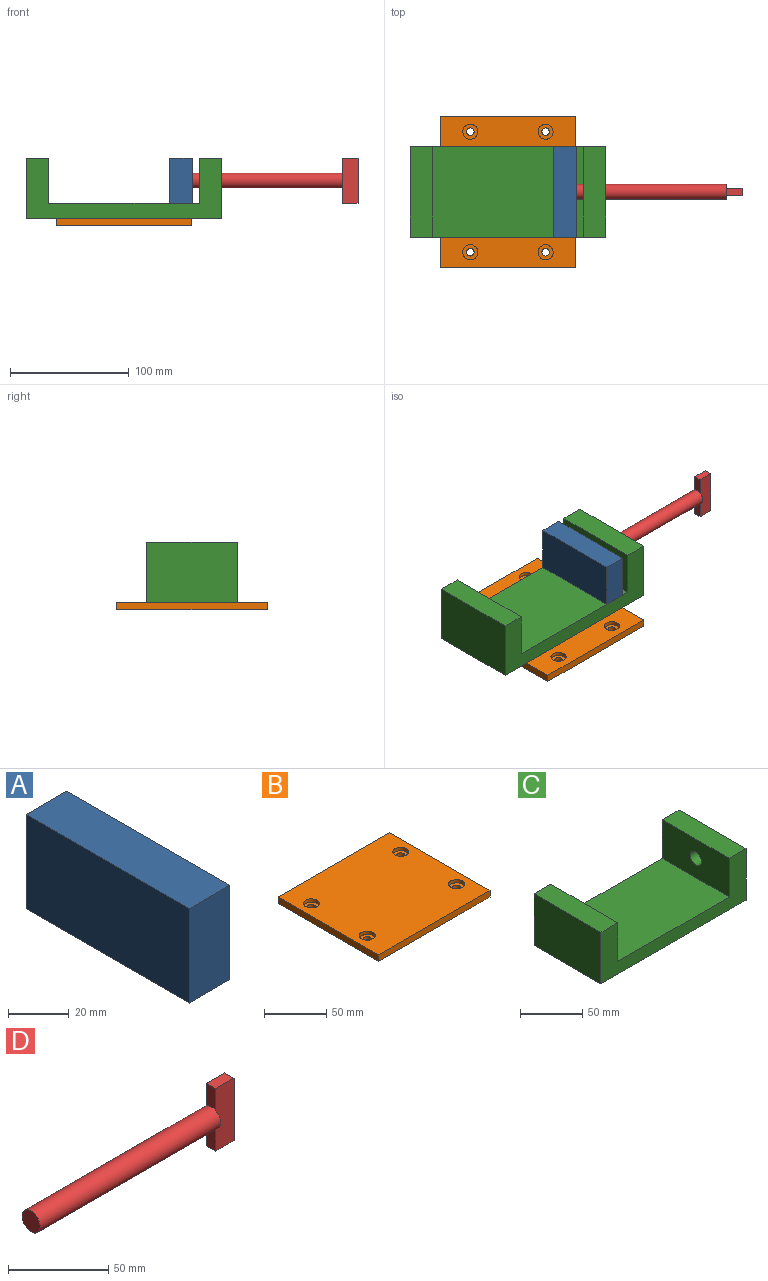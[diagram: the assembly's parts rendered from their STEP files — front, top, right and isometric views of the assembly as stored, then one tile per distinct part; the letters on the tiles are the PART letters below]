
ASSEMBLY  parts=4 mates=4
PART A: 6 faces, bbox 19.1x76.2x38.1 mm
  f0: plane 76.2x19.05mm, normal (0,0,1), area 1451.6mm2, adj f1,f3,f4,f5
  f1: plane 38.1x19.05mm, normal (0,-1,0), area 725.8mm2, adj f0,f2,f4,f5
  f2: plane 76.2x19.05mm, normal (0,0,-1), area 1451.6mm2, adj f1,f3,f4,f5
  f3: plane 38.1x19.05mm, normal (0,1,0), area 725.8mm2, adj f0,f2,f4,f5
  f4: plane 76.2x38.1mm, normal (1,0,0), area 2903.2mm2, adj f0,f1,f2,f3
  f5: plane 76.2x38.1mm, normal (-1,0,0), area 2903.2mm2, adj f0,f1,f2,f3
PART B: 18 faces, bbox 127x114.3x6.4 mm
  f0: plane 114.3x6.35mm, normal (-1,0,0), area 725.8mm2, adj f1,f3,f4,f5
  f1: plane 127x6.35mm, normal (0,-1,0), area 806.5mm2, adj f0,f2,f4,f5
  f2: plane 114.3x6.35mm, normal (1,0,0), area 725.8mm2, adj f1,f3,f4,f5
  f3: plane 127x6.35mm, normal (0,1,0), area 806.5mm2, adj f0,f2,f4,f5
  f4: plane 127x114.3mm, normal (0,0,1), area 14009.4mm2, adj f0,f1,f2,f3,f8,f11,f14,f17
  f5: plane 127x114.3mm, normal (0,0,-1), area 14389.4mm2, adj f0,f1,f2,f3,f6,f9,f12,f15
  f6: cylinder r=3.17mm len=6.35mm, axis (0,0,1), area 63.3mm2, adj f5,f7
  f7: plane 12.7x12.7mm, normal (0,0,1), area 95mm2, adj f6,f8
  f8: cylinder r=6.35mm len=12.7mm, axis (0,0,1), area 126.7mm2, adj f4,f7
  f9: cylinder r=3.17mm len=6.35mm, axis (0,0,1), area 63.3mm2, adj f5,f10
  f10: plane 12.7x12.7mm, normal (0,0,1), area 95mm2, adj f9,f11
  f11: cylinder r=6.35mm len=12.7mm, axis (0,0,1), area 126.7mm2, adj f4,f10
  f12: cylinder r=3.17mm len=6.35mm, axis (0,0,1), area 63.3mm2, adj f5,f13
  f13: plane 12.7x12.7mm, normal (0,0,1), area 95mm2, adj f12,f14
  f14: cylinder r=6.35mm len=12.7mm, axis (0,0,1), area 126.7mm2, adj f4,f13
  f15: cylinder r=3.17mm len=6.35mm, axis (0,0,1), area 63.3mm2, adj f5,f16
  f16: plane 12.7x12.7mm, normal (0,0,1), area 95mm2, adj f15,f17
  f17: cylinder r=6.35mm len=12.7mm, axis (0,0,1), area 126.7mm2, adj f4,f16
PART C: 11 faces, bbox 165.1x76.2x50.8 mm
  f0: plane 127x76.2mm, normal (0,0,1), area 9677.4mm2, adj f1,f7,f8,f9
  f1: plane 76.2x38.1mm, normal (1,0,0), area 2903.2mm2, adj f0,f2,f8,f9
  f2: plane 76.2x19.05mm, normal (0,0,1), area 1451.6mm2, adj f1,f3,f8,f9
  f3: plane 76.2x50.8mm, normal (-1,0,0), area 3871mm2, adj f2,f4,f8,f9
  f4: plane 165.1x76.2mm, normal (0,0,-1), area 12580.6mm2, adj f3,f5,f8,f9
  f5: plane 76.2x50.8mm, normal (1,0,0), area 3744.3mm2, adj f4,f6,f8,f9,f10
  f6: plane 76.2x19.05mm, normal (0,0,1), area 1451.6mm2, adj f5,f7,f8,f9
  f7: plane 76.2x38.1mm, normal (-1,0,0), area 2776.5mm2, adj f0,f6,f8,f9,f10
  f8: plane 165.1x50.8mm, normal (0,-1,0), area 3548.4mm2, adj f0,f1,f2,f3,f4,f5,f6,f7
  f9: plane 165.1x50.8mm, normal (0,1,0), area 3548.4mm2, adj f0,f1,f2,f3,f4,f5,f6,f7
  f10: cylinder r=6.35mm len=19.05mm, axis (1,0,0), area 760.1mm2, adj f5,f7
PART D: 11 faces, bbox 139.7x12.7x38.1 mm
  f0: plane 11x3.18mm, normal (1,0,0), area 24.8mm2, adj f1,f10
  f1: cylinder r=6.35mm len=127mm, axis (-1,0,0), area 5067.1mm2, adj f0,f2,f3,f4,f5
  f2: plane 11x3.18mm, normal (1,0,0), area 24.8mm2, adj f1,f9
  f3: plane 12.7x12.7mm, normal (-1,0,0), area 126.7mm2, adj f1
  f4: plane 13.55x6.35mm, normal (-1,0,0), area 82.4mm2, adj f1,f8,f9,f10
  f5: plane 13.55x6.35mm, normal (-1,0,0), area 82.4mm2, adj f1,f6,f9,f10
  f6: plane 12.7x6.35mm, normal (0,0,-1), area 80.6mm2, adj f5,f7,f9,f10
  f7: plane 38.1x6.35mm, normal (1,0,0), area 241.9mm2, adj f6,f8,f9,f10
  f8: plane 12.7x6.35mm, normal (0,0,1), area 80.6mm2, adj f4,f7,f9,f10
  f9: plane 38.1x12.7mm, normal (0,-1,0), area 483.9mm2, adj f2,f4,f5,f6,f7,f8
  f10: plane 38.1x12.7mm, normal (0,1,0), area 483.9mm2, adj f0,f4,f5,f6,f7,f8
PLACE A t=(-23.52,-16.86,43.02)mm
PLACE B rot(axis=(0,0,1),90deg) t=(-71.54,-16.86,4.92)mm
PLACE C t=(-8.04,-16.86,23.97)mm fixed
PLACE D t=(-13.99,-16.86,43.02)mm
MATE planar C.f0 <-> A.f2  axis (0,0,1) through (-71.54,-16.86,23.97)mm
MATE revolute D.f1 <-> A.f4  axis (-1,0,0) through (-13.99,-16.86,43.02)mm
MATE fastened C.f4 <-> B.f4  axis (0,0,-1) through (-71.54,-16.86,11.27)mm
MATE slider D.f1 <-> C.f10  axis (-1,0,0) through (113.01,-16.86,43.02)mm
